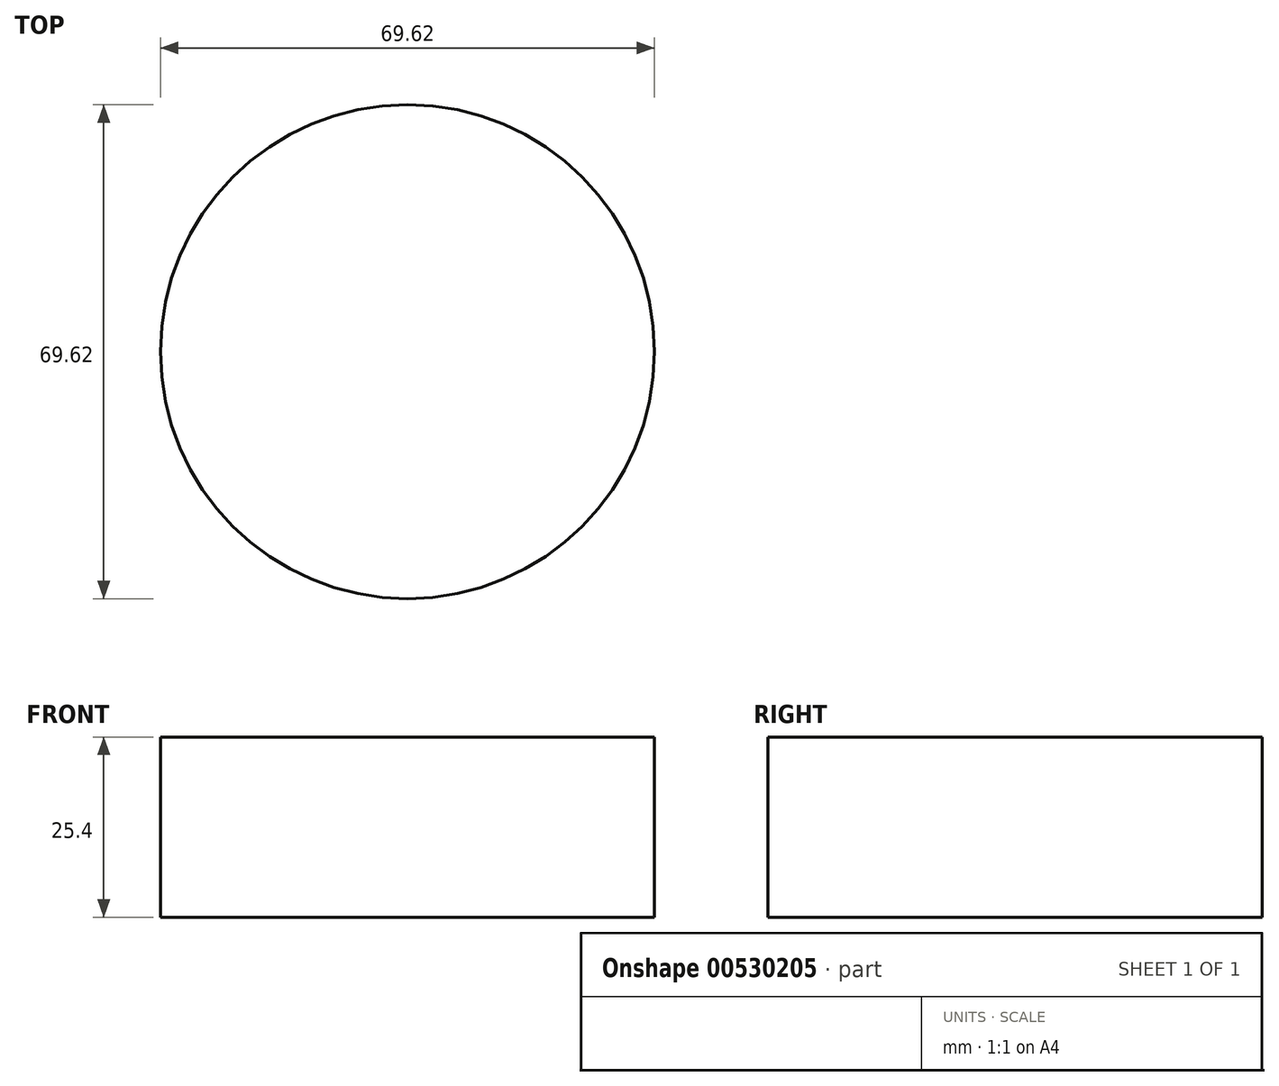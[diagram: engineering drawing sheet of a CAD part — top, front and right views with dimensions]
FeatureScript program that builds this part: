
annotation { "Feature Type Name" : "Feature", "Feature Type Description" : "" }
export const myFeature = defineFeature(function(context is Context, id is Id, definition is map)
    precondition{}
    {
        {
            var Q0;
            Q0=qCreatedBy(makeId("Top.planeOp"),FACE);
            var sketch = newSketch(context, id + "F0", { "sketchPlane" : qUnion([Q0])});
            skCircle(sketch, "E0", {"center": v(0, 0) * mm, "radius": 34.81 * mm});
            skSolve(sketch);
        }
        {
            var Q0;
            Q0=makeQuery(id+"F0.imprint","IMPRINT",FACE,{"disambiguationData":[TD([[makeQuery(id+"F0.imprint","IMPRINT",EDGE,{"derivedFrom":sQuery(id+"F0.wireOp",EDGE,"E0")}),1.0]])]});
            extrude(context, id + "F1", {"entities" : qUnion([Q0]), "depth" : 25.4 * mm, "offsetDistance" : 25.4 * mm});
        }
    });
